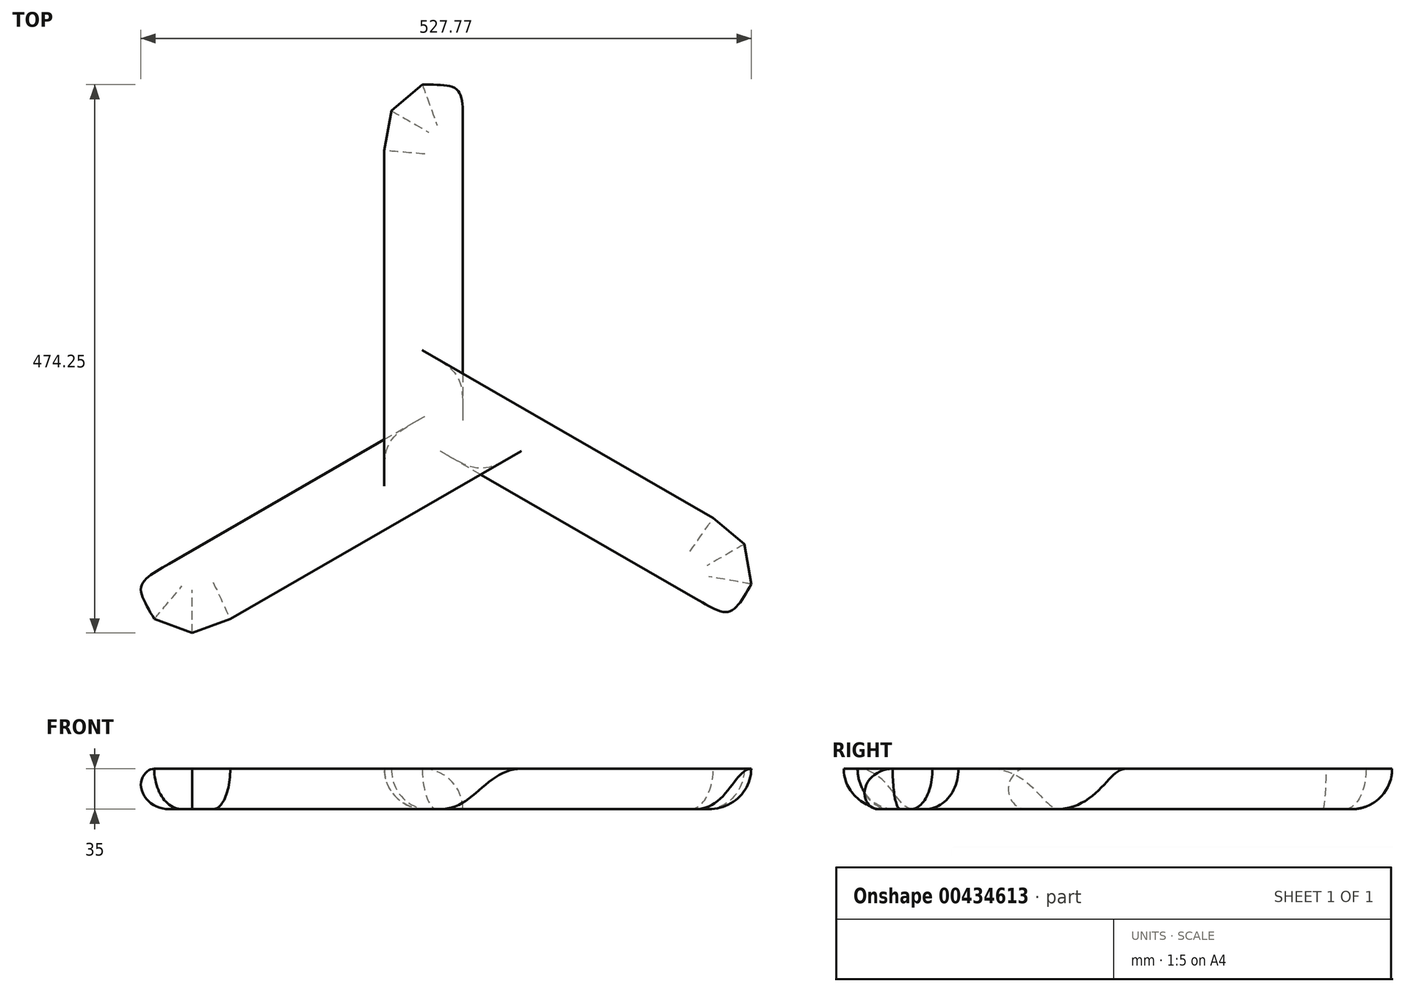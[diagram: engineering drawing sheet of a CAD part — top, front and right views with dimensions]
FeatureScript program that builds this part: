
annotation { "Feature Type Name" : "Feature", "Feature Type Description" : "" }
export const myFeature = defineFeature(function(context is Context, id is Id, definition is map)
    precondition{}
    {
        {
            var Q0;
            Q0=qCreatedBy(makeId("Top.planeOp"),FACE);
            var sketch = newSketch(context, id + "F0", { "sketchPlane" : qUnion([Q0])});
            skCircle(sketch, "E0.cCircle", {"center": v(0, 0) * mm, "radius": 48.08 * mm, "construction": true});
            skLineSegment(sketch, "E0.0", {"start": v(-17.5, 48.08) * mm, "end": v(17.5, 48.08) * mm});
            skLineSegment(sketch, "E0.1", {"start": v(17.5, 48.08) * mm, "end": v(44.31, 25.58) * mm});
            skLineSegment(sketch, "E0.2", {"start": v(44.31, 25.58) * mm, "end": v(50.39, -8.88) * mm});
            skLineSegment(sketch, "E0.3", {"start": v(50.39, -8.88) * mm, "end": v(32.89, -39.2) * mm});
            skLineSegment(sketch, "E0.4", {"start": v(32.89, -39.2) * mm, "end": v(0, -51.17) * mm});
            skLineSegment(sketch, "E0.5", {"start": v(0, -51.17) * mm, "end": v(-32.89, -39.2) * mm});
            skLineSegment(sketch, "E0.6", {"start": v(-32.89, -39.2) * mm, "end": v(-50.39, -8.88) * mm});
            skLineSegment(sketch, "E0.7", {"start": v(-50.39, -8.88) * mm, "end": v(-44.31, 25.58) * mm});
            skLineSegment(sketch, "E0.8", {"start": v(-44.31, 25.58) * mm, "end": v(-17.5, 48.08) * mm});
            skPoint(sketch, "E0.0.midPoint", {"position": v(0, 48.08) * mm});
            skSolve(sketch);
        }
        {
            var Q0;
            Q0=makeQuery(id+"F0.imprint","IMPRINT",FACE,{"disambiguationData":[TD([[makeQuery(id+"F0.imprint","IMPRINT",EDGE,{"derivedFrom":sQuery(id+"F0.wireOp",EDGE,"E0.0")}),-1.0]])]});
            extrude(context, id + "F1", {"entities" : qUnion([Q0]), "depth" : 35 * mm});
        }
        {
            var Q0;
            Q0=makeQuery(id+"F1.opExtrude","SWEPT_FACE",FACE,{"disambiguationData":[OSD([sQuery(id+"F0.wireOp",EDGE,"E0.3")])]});
            var Q1;
            Q1=makeQuery(id+"F1.opExtrude","SWEPT_FACE",FACE,{"disambiguationData":[OSD([sQuery(id+"F0.wireOp",EDGE,"E0.2")])]});
            var Q2;
            Q2=makeQuery(id+"F1.opExtrude","SWEPT_FACE",FACE,{"disambiguationData":[OSD([sQuery(id+"F0.wireOp",EDGE,"E0.1")])]});
            extrude(context, id + "F2", {"entities" : qUnion([Q0, Q1, Q2]), "operationType" : NewBodyOperationType.ADD, "depth" : 250 * mm});
        }
        {
            var Q0;
            Q0=makeQuery(id+"F1.opExtrude","SWEPT_FACE",FACE,{"disambiguationData":[OSD([sQuery(id+"F0.wireOp",EDGE,"E0.0")])]});
            var Q1;
            Q1=makeQuery(id+"F1.opExtrude","SWEPT_FACE",FACE,{"disambiguationData":[OSD([sQuery(id+"F0.wireOp",EDGE,"E0.8")])]});
            var Q2;
            Q2=makeQuery(id+"F1.opExtrude","SWEPT_FACE",FACE,{"disambiguationData":[OSD([sQuery(id+"F0.wireOp",EDGE,"E0.7")])]});
            extrude(context, id + "F3", {"entities" : qUnion([Q0, Q1, Q2]), "operationType" : NewBodyOperationType.ADD, "depth" : 250 * mm});
        }
        {
            var Q0;
            Q0=makeQuery(id+"F1.opExtrude","SWEPT_FACE",FACE,{"disambiguationData":[OSD([sQuery(id+"F0.wireOp",EDGE,"E0.6")])]});
            var Q1;
            Q1=makeQuery(id+"F1.opExtrude","SWEPT_FACE",FACE,{"disambiguationData":[OSD([sQuery(id+"F0.wireOp",EDGE,"E0.5")])]});
            var Q2;
            Q2=makeQuery(id+"F1.opExtrude","SWEPT_FACE",FACE,{"disambiguationData":[OSD([sQuery(id+"F0.wireOp",EDGE,"E0.4")])]});
            extrude(context, id + "F4", {"entities" : qUnion([Q0, Q1, Q2]), "operationType" : NewBodyOperationType.ADD, "depth" : 250 * mm});
        }
        {
            var Q0;
            {var subQ0=sQuery(id+"F0.wireOp",EDGE,"E0.1");var subQ1=sQuery(id+"F0.wireOp",EDGE,"E0.0");var subQ2=makeQuery(id+"F1.opExtrude","CAP_VERTEX",VERTEX,{"disambiguationData":[OSD([subQ1,subQ0])],"isStart":false});Q0=makeQuery(id+"F3.opExtrude","SWEPT_EDGE",EDGE,{"disambiguationData":[OSD([subQ1,subQ0]),TDD([makeQuery(id+"F2.boolean.opBoolean","MERGE",VERTEX,{"derivedFrom":[subQ2,makeQuery(id+"F2.opExtrude","CAP_VERTEX",VERTEX,{"disambiguationData":[OSD([subQ1,subQ0]),TDD([subQ2]),OD(0.0)],"isStart":false})]})])]});}
            var Q1;
            {var subQ0=sQuery(id+"F0.wireOp",EDGE,"E0.4");var subQ1=sQuery(id+"F0.wireOp",EDGE,"E0.3");Q1=makeQuery(id+"F2.opExtrude","SWEPT_EDGE",EDGE,{"disambiguationData":[OSD([subQ1,subQ0]),TDD([makeQuery(id+"F1.opExtrude","CAP_VERTEX",VERTEX,{"disambiguationData":[OSD([subQ1,subQ0])],"isStart":false})])]});}
            var Q2;
            {var subQ0=sQuery(id+"F0.wireOp",EDGE,"E0.7");var subQ1=sQuery(id+"F0.wireOp",EDGE,"E0.6");var subQ2=makeQuery(id+"F1.opExtrude","CAP_VERTEX",VERTEX,{"disambiguationData":[OSD([subQ1,subQ0])],"isStart":false});Q2=makeQuery(id+"F4.opExtrude","SWEPT_EDGE",EDGE,{"disambiguationData":[OSD([subQ1,subQ0]),TDD([makeQuery(id+"F3.boolean.opBoolean","MERGE",VERTEX,{"derivedFrom":[subQ2,makeQuery(id+"F3.opExtrude","CAP_VERTEX",VERTEX,{"disambiguationData":[OSD([subQ1,subQ0]),TDD([subQ2]),OD(0.0)],"isStart":false})]})])]});}
            fillet(context, id + "F5", {"entities" : qUnion([Q0, Q1, Q2]), "radius" : 35 * mm, "tangentPropagation" : true, "allowEdgeOverflow" : false});
        }
        {
            var Q0;
            {var subQ0=sQuery(id+"F0.wireOp",EDGE,"E0.4");var subQ1=sQuery(id+"F0.wireOp",EDGE,"E0.3");var subQ2=makeQuery(id+"F1.opExtrude","CAP_VERTEX",VERTEX,{"disambiguationData":[OSD([subQ1,subQ0])],"isStart":true});Q0=makeQuery(id+"F4.opExtrude","SWEPT_EDGE",EDGE,{"disambiguationData":[OSD([subQ1,subQ0]),TDD([makeQuery(id+"F2.boolean.opBoolean","MERGE",VERTEX,{"derivedFrom":[subQ2,makeQuery(id+"F2.opExtrude","CAP_VERTEX",VERTEX,{"disambiguationData":[OSD([subQ1,subQ0]),TDD([subQ2])],"isStart":true})]})])]});}
            var Q1;
            {var subQ0=sQuery(id+"F0.wireOp",EDGE,"E0.7");var subQ1=sQuery(id+"F0.wireOp",EDGE,"E0.6");Q1=makeQuery(id+"F3.opExtrude","SWEPT_EDGE",EDGE,{"disambiguationData":[OSD([subQ1,subQ0]),TDD([makeQuery(id+"F1.opExtrude","CAP_VERTEX",VERTEX,{"disambiguationData":[OSD([subQ1,subQ0])],"isStart":true})])]});}
            var Q2;
            {var subQ0=sQuery(id+"F0.wireOp",EDGE,"E0.1");var subQ1=sQuery(id+"F0.wireOp",EDGE,"E0.0");Q2=makeQuery(id+"F2.opExtrude","SWEPT_EDGE",EDGE,{"disambiguationData":[OSD([subQ1,subQ0]),TDD([makeQuery(id+"F1.opExtrude","CAP_VERTEX",VERTEX,{"disambiguationData":[OSD([subQ1,subQ0])],"isStart":true})])]});}
            var Q3;
            {var subQ0=sQuery(id+"F0.wireOp",EDGE,"E0.1");Q3=makeQuery(id+"F2.opExtrude","CAP_EDGE",EDGE,{"disambiguationData":[OSD([subQ0]),TDD([makeQuery(id+"F1.opExtrude","CAP_EDGE",EDGE,{"disambiguationData":[OSD([subQ0])],"isStart":true})]),OD(1.0)],"isStart":false});}
            var Q4;
            {var subQ0=sQuery(id+"F0.wireOp",EDGE,"E0.2");Q4=makeQuery(id+"F2.opExtrude","CAP_EDGE",EDGE,{"disambiguationData":[OSD([subQ0]),TDD([makeQuery(id+"F1.opExtrude","CAP_EDGE",EDGE,{"disambiguationData":[OSD([subQ0])],"isStart":true})]),OD(1.0)],"isStart":false});}
            var Q5;
            {var subQ0=sQuery(id+"F0.wireOp",EDGE,"E0.3");Q5=makeQuery(id+"F2.opExtrude","CAP_EDGE",EDGE,{"disambiguationData":[OSD([subQ0]),TDD([makeQuery(id+"F1.opExtrude","CAP_EDGE",EDGE,{"disambiguationData":[OSD([subQ0])],"isStart":true})])],"isStart":false});}
            var Q6;
            {var subQ0=sQuery(id+"F0.wireOp",EDGE,"E0.4");Q6=makeQuery(id+"F4.opExtrude","CAP_EDGE",EDGE,{"disambiguationData":[OSD([subQ0]),TDD([makeQuery(id+"F1.opExtrude","CAP_EDGE",EDGE,{"disambiguationData":[OSD([subQ0])],"isStart":true})]),OD(0.0)],"isStart":false});}
            var Q7;
            {var subQ0=sQuery(id+"F0.wireOp",EDGE,"E0.5");Q7=makeQuery(id+"F4.opExtrude","CAP_EDGE",EDGE,{"disambiguationData":[OSD([subQ0]),TDD([makeQuery(id+"F1.opExtrude","CAP_EDGE",EDGE,{"disambiguationData":[OSD([subQ0])],"isStart":true})]),OD(0.0)],"isStart":false});}
            var Q8;
            {var subQ0=sQuery(id+"F0.wireOp",EDGE,"E0.6");Q8=makeQuery(id+"F4.opExtrude","CAP_EDGE",EDGE,{"disambiguationData":[OSD([subQ0]),TDD([makeQuery(id+"F1.opExtrude","CAP_EDGE",EDGE,{"disambiguationData":[OSD([subQ0])],"isStart":true})])],"isStart":false});}
            var Q9;
            {var subQ0=sQuery(id+"F0.wireOp",EDGE,"E0.7");Q9=makeQuery(id+"F3.opExtrude","CAP_EDGE",EDGE,{"disambiguationData":[OSD([subQ0]),TDD([makeQuery(id+"F1.opExtrude","CAP_EDGE",EDGE,{"disambiguationData":[OSD([subQ0])],"isStart":true})]),OD(1.0)],"isStart":false});}
            var Q10;
            {var subQ0=sQuery(id+"F0.wireOp",EDGE,"E0.8");Q10=makeQuery(id+"F3.opExtrude","CAP_EDGE",EDGE,{"disambiguationData":[OSD([subQ0]),TDD([makeQuery(id+"F1.opExtrude","CAP_EDGE",EDGE,{"disambiguationData":[OSD([subQ0])],"isStart":true})]),OD(1.0)],"isStart":false});}
            var Q11;
            {var subQ0=sQuery(id+"F0.wireOp",EDGE,"E0.0");Q11=makeQuery(id+"F3.opExtrude","CAP_EDGE",EDGE,{"disambiguationData":[OSD([subQ0]),TDD([makeQuery(id+"F1.opExtrude","CAP_EDGE",EDGE,{"disambiguationData":[OSD([subQ0])],"isStart":true})])],"isStart":false});}
            fillet(context, id + "F6", {"entities" : qUnion([Q0, Q1, Q2, Q3, Q4, Q5, Q6, Q7, Q8, Q9, Q10, Q11]), "radius" : 35 * mm, "tangentPropagation" : true, "allowEdgeOverflow" : false});
        }
    });
